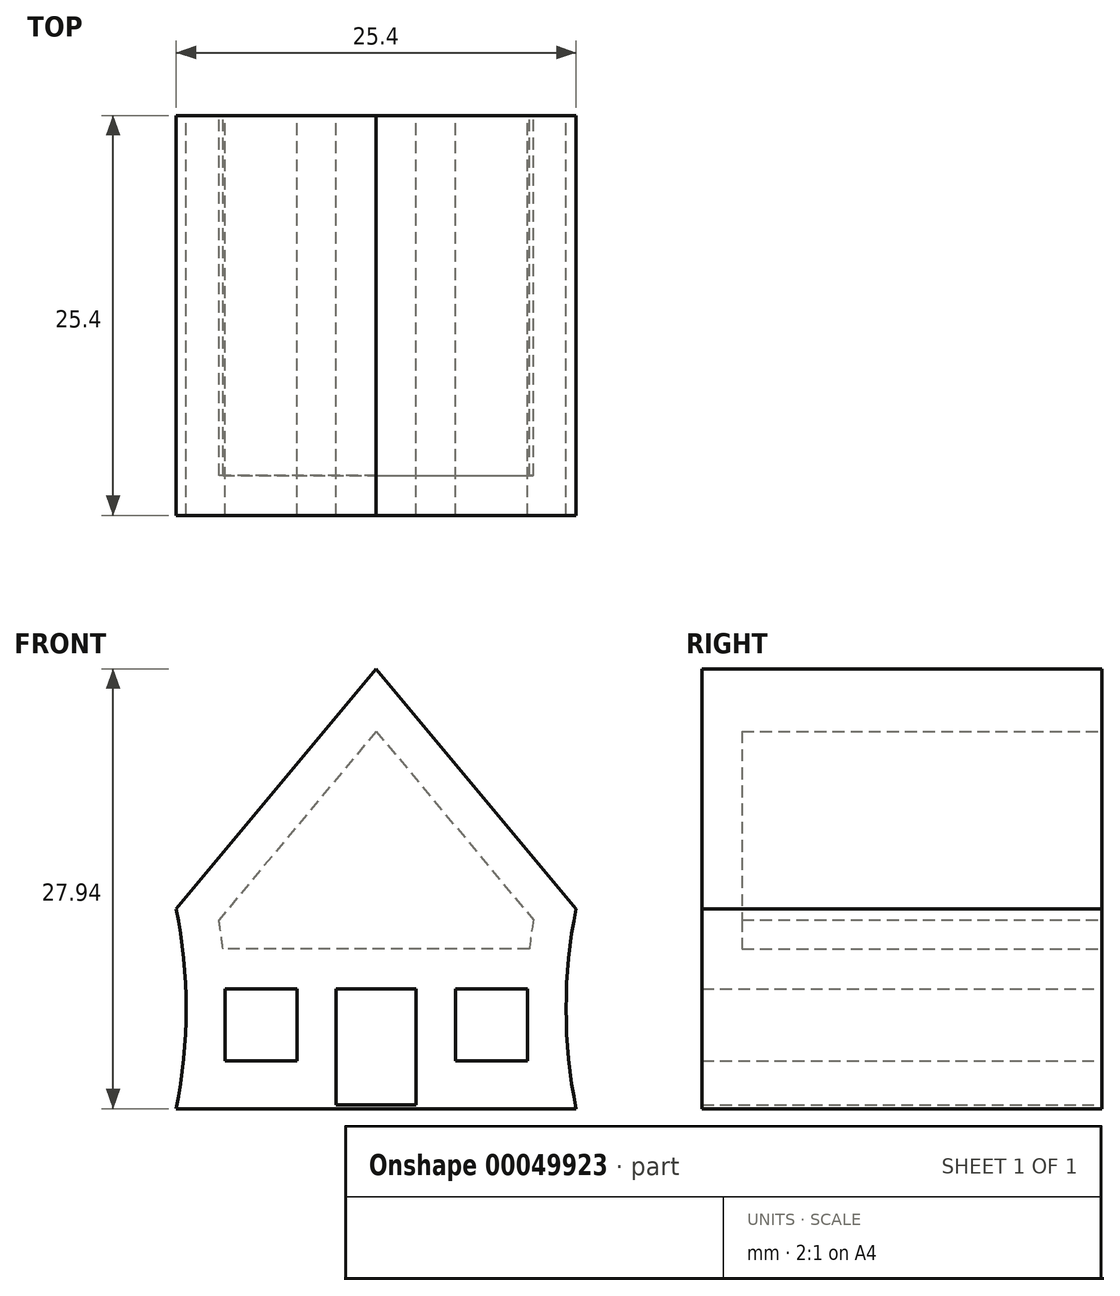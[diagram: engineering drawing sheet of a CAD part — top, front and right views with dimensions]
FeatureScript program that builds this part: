
annotation { "Feature Type Name" : "Feature", "Feature Type Description" : "" }
export const myFeature = defineFeature(function(context is Context, id is Id, definition is map)
    precondition{}
    {
        {
            var Q0;
            Q0=qCreatedBy(makeId("Front.planeOp"),FACE);
            var sketch = newSketch(context, id + "F0", { "sketchPlane" : qUnion([Q0])});
            skLineSegment(sketch, "E0", {"start": v(0, 0) * mm, "end": v(25.4, 0) * mm});
            skLineSegment(sketch, "E1", {"start": v(25.4, 12.7) * mm, "end": v(0, 12.7) * mm});
            skLineSegment(sketch, "E2", {"start": v(0, 6.35) * mm, "end": v(0.64, 6.35) * mm});
            skLineSegment(sketch, "E3", {"start": v(25.4, 6.35) * mm, "end": v(24.77, 6.35) * mm});
            skArc(sketch, "E4", {"start": v(0, 0) * mm, "mid": v(0.64, 6.35) * mm, "end": v(0, 12.7) * mm});
            skArc(sketch, "E5", {"start": v(25.4, 12.7) * mm, "mid": v(24.77, 6.35) * mm, "end": v(25.4, 0) * mm});
            skLineSegment(sketch, "E6", {"start": v(12.7, 27.94) * mm, "end": v(0, 12.7) * mm});
            skLineSegment(sketch, "E7", {"start": v(12.7, 27.94) * mm, "end": v(25.4, 12.7) * mm});
            skLineSegment(sketch, "E8", {"start": v(10.16, 7.62) * mm, "end": v(0.6, 7.62) * mm, "construction": true});
            skLineSegment(sketch, "E9", {"start": v(0.6, 7.62) * mm, "end": v(24.8, 7.62) * mm, "construction": true});
            skLineSegment(sketch, "E10", {"start": v(5.38, 7.62) * mm, "end": v(5.38, 3.05) * mm});
            skLineSegment(sketch, "E11", {"start": v(5.38, 3.05) * mm, "end": v(7.67, 3.05) * mm});
            skLineSegment(sketch, "E12", {"start": v(5.38, 3.05) * mm, "end": v(3.1, 3.05) * mm});
            skLineSegment(sketch, "E13", {"start": v(3.1, 3.05) * mm, "end": v(3.1, 7.62) * mm});
            skLineSegment(sketch, "E14", {"start": v(3.1, 7.62) * mm, "end": v(5.38, 7.62) * mm});
            skLineSegment(sketch, "E15", {"start": v(7.67, 3.05) * mm, "end": v(7.67, 7.62) * mm});
            skLineSegment(sketch, "E16", {"start": v(7.67, 7.62) * mm, "end": v(5.38, 7.62) * mm});
            skLineSegment(sketch, "E17", {"start": v(5.38, 7.62) * mm, "end": v(10.16, 7.62) * mm});
            skLineSegment(sketch, "E18", {"start": v(15.24, 7.62) * mm, "end": v(20.02, 7.62) * mm});
            skLineSegment(sketch, "E19", {"start": v(20.02, 7.62) * mm, "end": v(20.02, 3.05) * mm});
            skLineSegment(sketch, "E20", {"start": v(20.02, 3.05) * mm, "end": v(17.73, 3.05) * mm});
            skLineSegment(sketch, "E21", {"start": v(20.02, 3.05) * mm, "end": v(22.3, 3.05) * mm});
            skLineSegment(sketch, "E22", {"start": v(22.3, 3.05) * mm, "end": v(22.3, 7.62) * mm});
            skLineSegment(sketch, "E23", {"start": v(22.3, 7.62) * mm, "end": v(20.02, 7.62) * mm});
            skLineSegment(sketch, "E24", {"start": v(17.73, 3.05) * mm, "end": v(17.73, 7.62) * mm});
            skLineSegment(sketch, "E25", {"start": v(17.73, 7.62) * mm, "end": v(20.02, 7.62) * mm});
            skLineSegment(sketch, "E26", {"start": v(12.7, 7.62) * mm, "end": v(12.7, 27.94) * mm});
            skLineSegment(sketch, "E27", {"start": v(10.16, 7.62) * mm, "end": v(15.24, 7.62) * mm});
            skLineSegment(sketch, "E28", {"start": v(10.16, 7.62) * mm, "end": v(10.16, 0.25) * mm});
            skLineSegment(sketch, "E29", {"start": v(10.16, 0.25) * mm, "end": v(15.24, 0.25) * mm});
            skLineSegment(sketch, "E30", {"start": v(15.24, 7.62) * mm, "end": v(15.24, 0.25) * mm});
            skLineSegment(sketch, "E31", {"start": v(17.73, 7.62) * mm, "end": v(17.73, 12.7) * mm, "construction": true});
            skLineSegment(sketch, "E32", {"start": v(17.73, 12.7) * mm, "end": v(22.3, 7.62) * mm, "construction": true});
            skLineSegment(sketch, "E33", {"start": v(22.3, 7.62) * mm, "end": v(22.3, 12.7) * mm, "construction": true});
            skLineSegment(sketch, "E34", {"start": v(22.3, 12.7) * mm, "end": v(17.73, 7.62) * mm, "construction": true});
            skLineSegment(sketch, "E35", {"start": v(17.73, 10.16) * mm, "end": v(22.3, 10.16) * mm, "construction": true});
            skLineSegment(sketch, "E36", {"start": v(17.73, 10.16) * mm, "end": v(17.73, 12.7) * mm});
            skLineSegment(sketch, "E37", {"start": v(22.3, 10.16) * mm, "end": v(22.3, 12.7) * mm});
            skLineSegment(sketch, "E38", {"start": v(17.73, 9.1) * mm, "end": v(22.3, 9.1) * mm});
            skLineSegment(sketch, "E39", {"start": v(2.25, 12.7) * mm, "end": v(2.25, 0) * mm});
            skSolve(sketch);
        }
        {
            var Q0;
            Q0 = qSketchRegion(id + "F0", true);
            extrude(context, id + "F1", {"entities" : qUnion([Q0]), "depth" : 25.4 * mm});
        }
        {
            var Q0;
            Q0=makeQuery(id+"F1.opExtrude","CAP_FACE",FACE,{"disambiguationData":[OSD([sQuery(id+"F0.wireOp",EDGE,"E0"),sQuery(id+"F0.wireOp",EDGE,"E4"),sQuery(id+"F0.wireOp",EDGE,"E5"),sQuery(id+"F0.wireOp",EDGE,"E6"),sQuery(id+"F0.wireOp",EDGE,"E7"),sQuery(id+"F0.wireOp",EDGE,"E11"),sQuery(id+"F0.wireOp",EDGE,"E12"),sQuery(id+"F0.wireOp",EDGE,"E13"),sQuery(id+"F0.wireOp",EDGE,"E14"),sQuery(id+"F0.wireOp",EDGE,"E15"),sQuery(id+"F0.wireOp",EDGE,"E17"),sQuery(id+"F0.wireOp",EDGE,"E20"),sQuery(id+"F0.wireOp",EDGE,"E21"),sQuery(id+"F0.wireOp",EDGE,"E22"),sQuery(id+"F0.wireOp",EDGE,"E23"),sQuery(id+"F0.wireOp",EDGE,"E24"),sQuery(id+"F0.wireOp",EDGE,"E25"),sQuery(id+"F0.wireOp",EDGE,"E27"),sQuery(id+"F0.wireOp",EDGE,"E28"),sQuery(id+"F0.wireOp",EDGE,"E29"),sQuery(id+"F0.wireOp",EDGE,"E30")])],"isStart":true});
            shell(context, id + "F2", {"entities" : qUnion([Q0]), "thickness" : 2.54 * mm});
        }
    });
